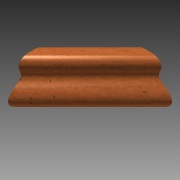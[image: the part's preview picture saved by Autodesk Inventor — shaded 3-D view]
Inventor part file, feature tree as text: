
AUTODESK INVENTOR PART (.ipt)
format: ipt  version: 2015 (Build 190159000, 159)  size: 156,160 bytes
history: native  units: in
note: dims shown in document units (in); Inventor stores cm internally (conversion verified against a paired STEP export)
features: sketch x2, loft x1
ambient origin geometry x8: Origin, YZ Plane, XZ Plane, XY Plane, X Axis, Y Axis, Z Axis, Center Point
bodies: Solid1 (feature_tree)
feature tree (3):
  loft  "Loft1"
  sketch  "Sketch1"  dims[d0=0.1in d1=0.1in]
  sketch  "Sketch2"  dims[d2=2.75in d3=1.0in d4=1.0in d5=0.5in d6=0.6in d7=0.25in d8=0.5in d9=0.5in d10=0.5in d11=0.25in d12=0.1in d13=0.1in d15=1.0in d16=1.0in d17=0.5in d18=0.6in d19=0.25in d20=0.5in d21=0.5in d22=0.5in d23=0.25in d24=2.75in d25=0.0in d26=90.0deg d27=0.0in d28=90.0deg]
